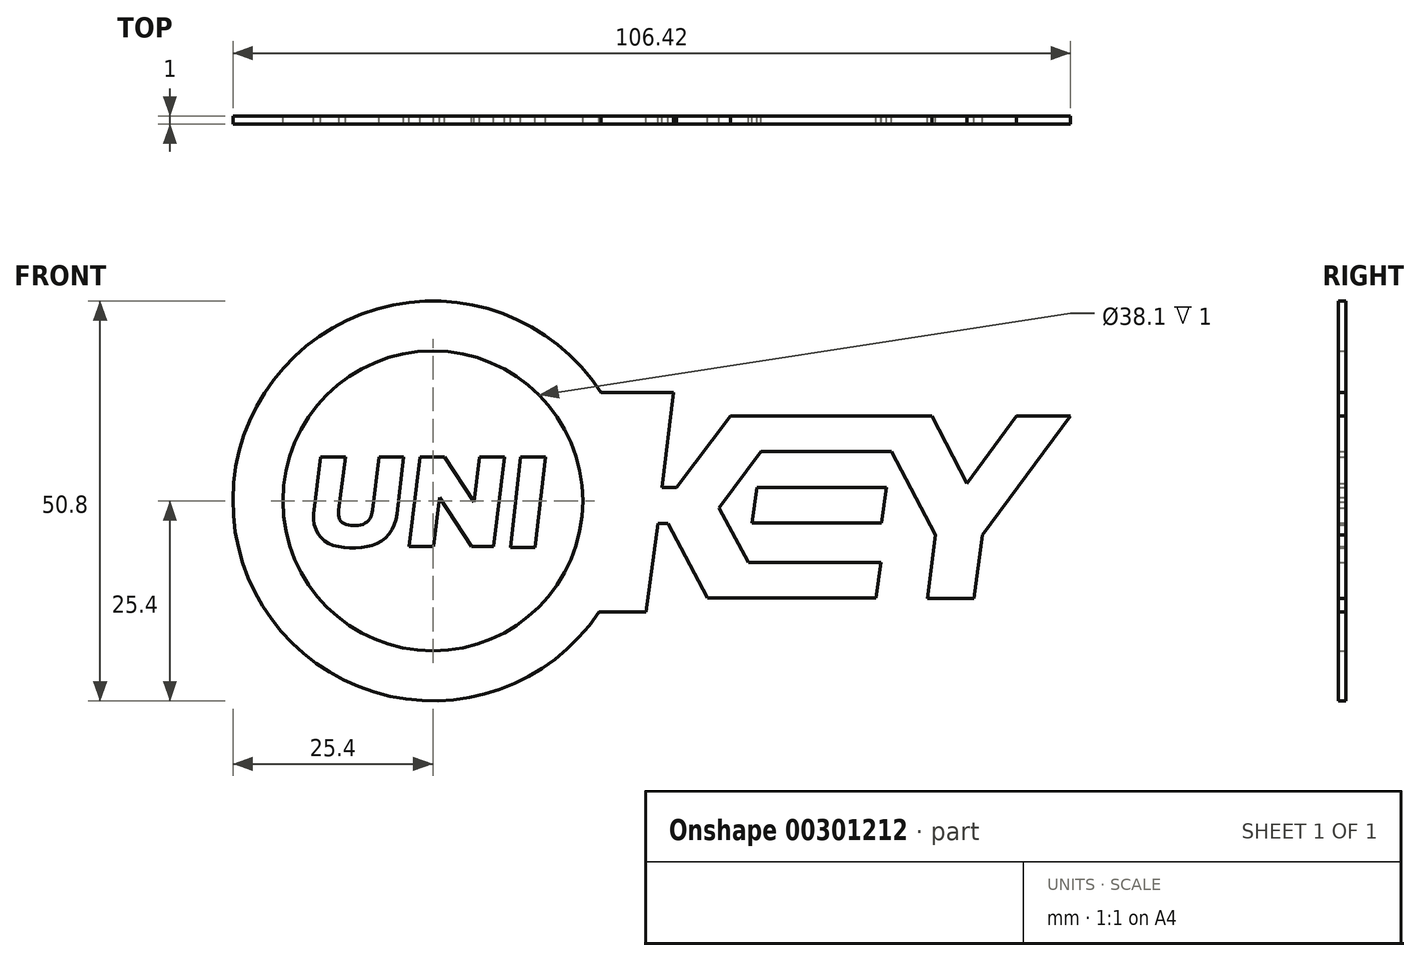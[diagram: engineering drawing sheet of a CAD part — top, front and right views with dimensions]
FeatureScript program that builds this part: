
annotation { "Feature Type Name" : "Feature", "Feature Type Description" : "" }
export const myFeature = defineFeature(function(context is Context, id is Id, definition is map)
    precondition{}
    {
        {
            var Q0;
            Q0=qCreatedBy(makeId("Front.planeOp"),FACE);
            var sketch = newSketch(context, id + "F0", { "sketchPlane" : qUnion([Q0])});
            skSolve(sketch);
        }
        {
            var Q0;
            Q0=qCreatedBy(makeId("Front.planeOp"),FACE);
            var sketch = newSketch(context, id + "F1", { "sketchPlane" : qUnion([Q0])});
            skLineSegment(sketch, "E0.0", {"start": v(106.6, 50.8) * mm, "end": v(0, 50.8) * mm});
            skPoint(sketch, "E1.0", {"position": v(0, 25.4) * mm});
            skLineSegment(sketch, "E2.0", {"start": v(0, 0) * mm, "end": v(106.6, 0) * mm});
            skCircle(sketch, "E3", {"center": v(25.4, 25.4) * mm, "radius": 25.4 * mm});
            skPoint(sketch, "E3.second.point", {"position": v(25.4, 50.8) * mm});
            skPoint(sketch, "E3.third.point", {"position": v(25.4, 0) * mm});
            skCircle(sketch, "E4", {"center": v(25.4, 25.4) * mm, "radius": 19.05 * mm});
            skLineSegment(sketch, "E5", {"start": v(46.75, 39.16) * mm, "end": v(55.96, 39.16) * mm});
            skLineSegment(sketch, "E6", {"start": v(55.96, 39.16) * mm, "end": v(54.52, 27.13) * mm});
            skLineSegment(sketch, "E7", {"start": v(63.19, 36.2) * mm, "end": v(88.82, 36.2) * mm});
            skLineSegment(sketch, "E8", {"start": v(88.82, 36.2) * mm, "end": v(93.23, 27.6) * mm});
            skLineSegment(sketch, "E9", {"start": v(93.23, 27.6) * mm, "end": v(99.5, 36.2) * mm});
            skLineSegment(sketch, "E10", {"start": v(99.5, 36.2) * mm, "end": v(106.42, 36.2) * mm});
            skLineSegment(sketch, "E11", {"start": v(106.42, 36.2) * mm, "end": v(95.19, 21.06) * mm});
            skLineSegment(sketch, "E12", {"start": v(95.19, 21.06) * mm, "end": v(94.13, 13.05) * mm});
            skLineSegment(sketch, "E13", {"start": v(94.13, 13.05) * mm, "end": v(88.2, 13.05) * mm});
            skLineSegment(sketch, "E14", {"start": v(88.2, 13.05) * mm, "end": v(89.26, 21.06) * mm});
            skLineSegment(sketch, "E15", {"start": v(89.26, 21.06) * mm, "end": v(83.67, 31.67) * mm});
            skLineSegment(sketch, "E16", {"start": v(83.67, 31.67) * mm, "end": v(67.1, 31.67) * mm});
            skLineSegment(sketch, "E17", {"start": v(67.1, 31.67) * mm, "end": v(61.78, 24.5) * mm});
            skLineSegment(sketch, "E18", {"start": v(61.78, 24.5) * mm, "end": v(65.5, 17.57) * mm});
            skLineSegment(sketch, "E19", {"start": v(65.5, 17.57) * mm, "end": v(82.3, 17.57) * mm});
            skLineSegment(sketch, "E20", {"start": v(82.3, 17.57) * mm, "end": v(81.7, 13.1) * mm});
            skLineSegment(sketch, "E21", {"start": v(81.7, 13.1) * mm, "end": v(60.3, 13.1) * mm});
            skLineSegment(sketch, "E22", {"start": v(60.3, 13.1) * mm, "end": v(55.26, 22.53) * mm});
            skLineSegment(sketch, "E23", {"start": v(55.26, 22.53) * mm, "end": v(54, 22.53) * mm});
            skLineSegment(sketch, "E24", {"start": v(54, 22.53) * mm, "end": v(52.49, 11.28) * mm});
            skLineSegment(sketch, "E25", {"start": v(52.49, 11.28) * mm, "end": v(46.51, 11.28) * mm});
            skLineSegment(sketch, "E26", {"start": v(54.52, 27.13) * mm, "end": v(56.38, 27.13) * mm});
            skLineSegment(sketch, "E27", {"start": v(56.38, 27.13) * mm, "end": v(63.19, 36.2) * mm});
            skLineSegment(sketch, "E28", {"start": v(66.55, 27.08) * mm, "end": v(65.96, 22.6) * mm});
            skLineSegment(sketch, "E29", {"start": v(65.96, 22.6) * mm, "end": v(82.4, 22.6) * mm});
            skLineSegment(sketch, "E30", {"start": v(82.4, 22.6) * mm, "end": v(83, 27.08) * mm});
            skLineSegment(sketch, "E31", {"start": v(83, 27.08) * mm, "end": v(66.55, 27.08) * mm});
            skLineSegment(sketch, "E32", {"start": v(22.39, 19.63) * mm, "end": v(23.8, 30.97) * mm});
            skLineSegment(sketch, "E33", {"start": v(23.8, 30.97) * mm, "end": v(26.91, 30.97) * mm});
            skLineSegment(sketch, "E34", {"start": v(26.91, 30.97) * mm, "end": v(30.62, 25.3) * mm});
            skLineSegment(sketch, "E35", {"start": v(30.62, 25.3) * mm, "end": v(31.33, 30.97) * mm});
            skLineSegment(sketch, "E36", {"start": v(31.33, 30.97) * mm, "end": v(34.51, 30.97) * mm});
            skLineSegment(sketch, "E37", {"start": v(34.51, 30.97) * mm, "end": v(33.1, 19.63) * mm});
            skLineSegment(sketch, "E38", {"start": v(33.1, 19.63) * mm, "end": v(30.35, 19.63) * mm});
            skLineSegment(sketch, "E39", {"start": v(30.35, 19.63) * mm, "end": v(26.28, 25.87) * mm});
            skLineSegment(sketch, "E40", {"start": v(26.28, 25.87) * mm, "end": v(25.5, 19.63) * mm});
            skLineSegment(sketch, "E41", {"start": v(25.5, 19.63) * mm, "end": v(22.39, 19.63) * mm});
            skLineSegment(sketch, "E42", {"start": v(36.55, 30.97) * mm, "end": v(39.7, 30.97) * mm});
            skLineSegment(sketch, "E43", {"start": v(39.7, 30.97) * mm, "end": v(38.4, 19.49) * mm});
            skLineSegment(sketch, "E44", {"start": v(38.4, 19.49) * mm, "end": v(35.26, 19.49) * mm});
            skLineSegment(sketch, "E45", {"start": v(35.26, 19.49) * mm, "end": v(36.55, 30.97) * mm});
            skLineSegment(sketch, "E46", {"start": v(21.69, 30.97) * mm, "end": v(18.58, 30.97) * mm});
            skLineSegment(sketch, "E47", {"start": v(14.3, 30.97) * mm, "end": v(11.17, 30.97) * mm});
            skLineSegment(sketch, "E48", {"start": v(11.17, 30.97) * mm, "end": v(10.27, 23.75) * mm});
            skLineSegment(sketch, "E49", {"start": v(21.69, 30.97) * mm, "end": v(20.83, 23.75) * mm});
            skFitSpline(sketch, "E50", {"points": [v(10.27, 23.75) * mm, v(10.99, 21) * mm, v(13.2, 19.64) * mm, v(16.86, 19.56) * mm, v(19.54, 20.86) * mm, v(20.83, 23.75) * mm], "startDerivative": vector(-1.98, -15.87) * mm, "endDerivative": vector(1.96, 16.5) * mm});
            skLineSegment(sketch, "E51", {"start": v(14.3, 30.97) * mm, "end": v(13.46, 24.23) * mm});
            skLineSegment(sketch, "E52", {"start": v(18.58, 30.97) * mm, "end": v(17.74, 24.23) * mm});
            skFitSpline(sketch, "E53", {"points": [v(13.46, 24.23) * mm, v(13.64, 22.94) * mm, v(14.65, 22.37) * mm, v(16.2, 22.34) * mm, v(17.33, 23.05) * mm, v(17.74, 24.23) * mm], "startDerivative": vector(-0.9, -7.25) * mm, "endDerivative": vector(0.83, 6.63) * mm});
            skSolve(sketch);
        }
        {
            var Q0;
            Q0=makeQuery(id+"F1.imprint","IMPRINT",FACE,{"disambiguationData":[TD([[makeQuery(id+"F1.imprint","IMPRINT",EDGE,{"derivedFrom":sQuery(id+"F1.wireOp",EDGE,"E28")}),1.0]])]});
            var Q1;
            {var subQ1=sQuery(id+"F1.wireOp",EDGE,"E5");Q1=makeQuery(id+"F1.imprint","IMPRINT",FACE,{"disambiguationData":[TD([[makeQuery(id+"F1.imprint","IMPRINT",EDGE,{"derivedFrom":subQ1}),-1.0]])]});}
            var Q2;
            Q2=makeQuery(id+"F1.imprint","IMPRINT",FACE,{"disambiguationData":[TD([[makeQuery(id+"F1.imprint","IMPRINT",EDGE,{"derivedFrom":sQuery(id+"F1.wireOp",EDGE,"E4")}),-1.0]])]});
            var Q3;
            Q3=makeQuery(id+"F1.imprint","IMPRINT",FACE,{"disambiguationData":[TD([[makeQuery(id+"F1.imprint","IMPRINT",EDGE,{"derivedFrom":sQuery(id+"F1.wireOp",EDGE,"E32")}),-1.0]])]});
            var Q4;
            Q4=makeQuery(id+"F1.imprint","IMPRINT",FACE,{"disambiguationData":[TD([[makeQuery(id+"F1.imprint","IMPRINT",EDGE,{"derivedFrom":sQuery(id+"F1.wireOp",EDGE,"E46")}),1.0]])]});
            var Q5;
            Q5=makeQuery(id+"F1.imprint","IMPRINT",FACE,{"disambiguationData":[TD([[makeQuery(id+"F1.imprint","IMPRINT",EDGE,{"derivedFrom":sQuery(id+"F1.wireOp",EDGE,"E42")}),-1.0]])]});
            extrude(context, id + "F2", {"entities" : qUnion([Q0, Q1, Q2, Q3, Q4, Q5]), "depth" : 1 * mm});
        }
    });
